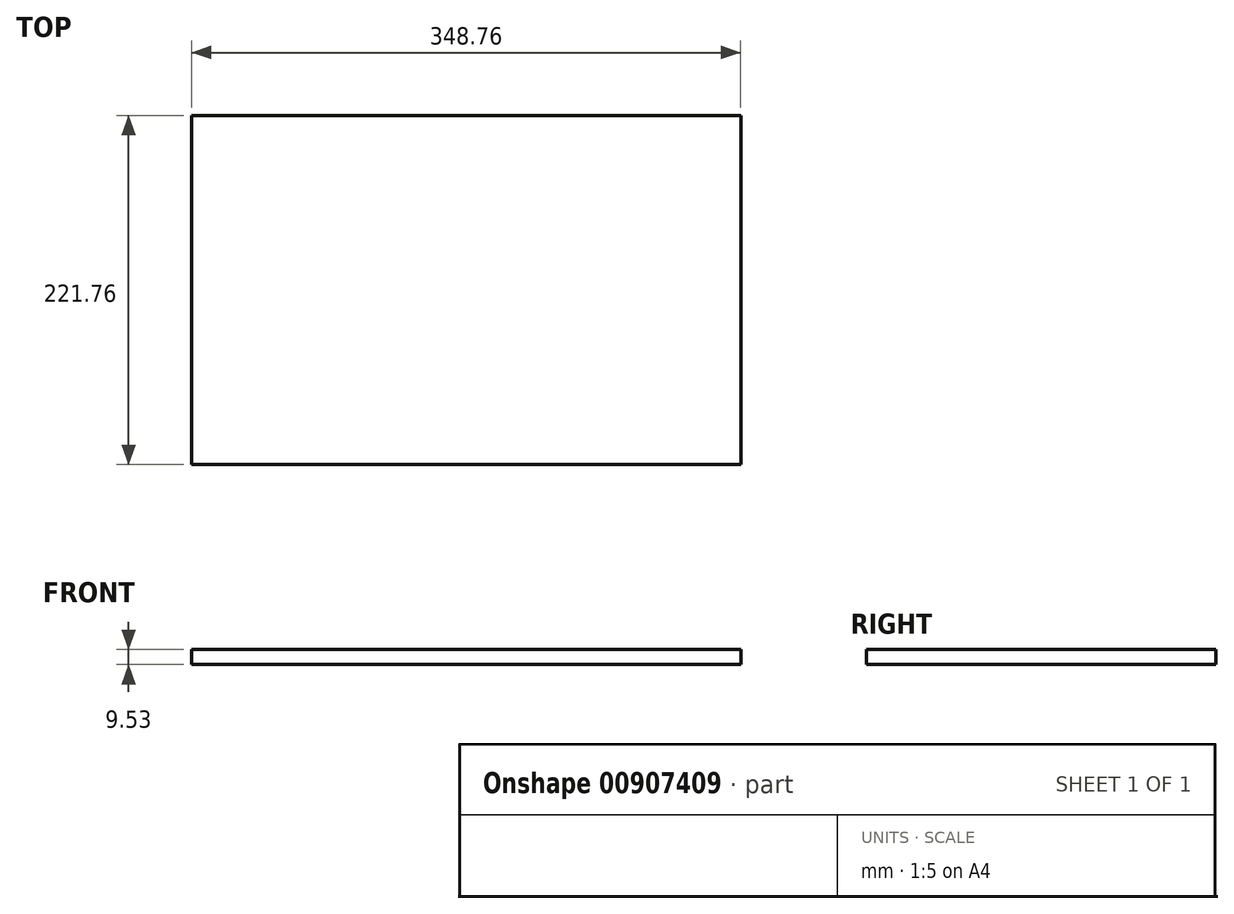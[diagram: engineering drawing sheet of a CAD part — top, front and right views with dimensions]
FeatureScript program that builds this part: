
annotation { "Feature Type Name" : "Feature", "Feature Type Description" : "" }
export const myFeature = defineFeature(function(context is Context, id is Id, definition is map)
    precondition{}
    {
        {
            var Q0;
            Q0=qCreatedBy(makeId("Top.planeOp"),FACE);
            var sketch = newSketch(context, id + "F0", { "sketchPlane" : qUnion([Q0])});
            skLineSegment(sketch, "E0.bottom", {"start": v(-177.8, 114.3) * mm, "end": v(177.8, 114.3) * mm, "construction": true});
            skLineSegment(sketch, "E0.top", {"start": v(-177.8, -114.3) * mm, "end": v(177.8, -114.3) * mm, "construction": true});
            skLineSegment(sketch, "E0.left", {"start": v(-177.8, 114.3) * mm, "end": v(-177.8, -114.3) * mm, "construction": true});
            skLineSegment(sketch, "E0.right", {"start": v(177.8, 114.3) * mm, "end": v(177.8, -114.3) * mm, "construction": true});
            skLineSegment(sketch, "E1.0", {"start": v(-174.38, 110.88) * mm, "end": v(174.38, 110.88) * mm});
            skLineSegment(sketch, "E1.1", {"start": v(-174.38, 110.88) * mm, "end": v(-174.38, -110.88) * mm});
            skLineSegment(sketch, "E1.2", {"start": v(-174.38, -110.88) * mm, "end": v(174.38, -110.88) * mm});
            skLineSegment(sketch, "E1.3", {"start": v(174.38, 110.88) * mm, "end": v(174.38, -110.88) * mm});
            skSolve(sketch);
        }
        {
            var Q0;
            Q0 = qSketchRegion(id + "F0", true);
            extrude(context, id + "F1", {"entities" : qUnion([Q0]), "depth" : 9.52 * mm, "offsetDistance" : 25.4 * mm});
        }
    });
